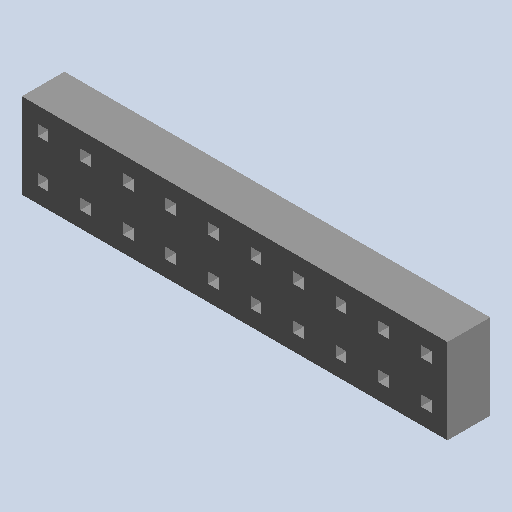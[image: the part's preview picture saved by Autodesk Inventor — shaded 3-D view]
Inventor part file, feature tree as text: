
AUTODESK INVENTOR PART (.ipt)
format: ipt  version: 2024.2 (Build 282272000, 272)  size: 177,664 bytes
history: native  units: mm (DEFAULTED — no unit token found)
features: other x7, extrude x1, sketch x1
ambient origin geometry x8: Origin, YZ Plane, XZ Plane, XY Plane, X Axis, Y Axis, Z Axis, Center Point
bodies: Solid1 (feature_tree)
feature tree (9):
  extrude  "Extrusion1"  TaperAngle=0.0deg  [1 undecoded]
  other  "0_XY"
  other  "0_YZ"
  other  "0_ZX"
  other  "0_X"
  other  "0_Y"
  other  "0_Z"
  other  "0_Center"
  sketch  "Sketch0"  dims[d0=2.0066mm d1=0.0mm d2=0.0mm]
note: 1 required parameter value undecoded (feature->parameter linkage not recoverable at this tier; creation-order binding heuristic only, values carry confidence <= 0.55)
